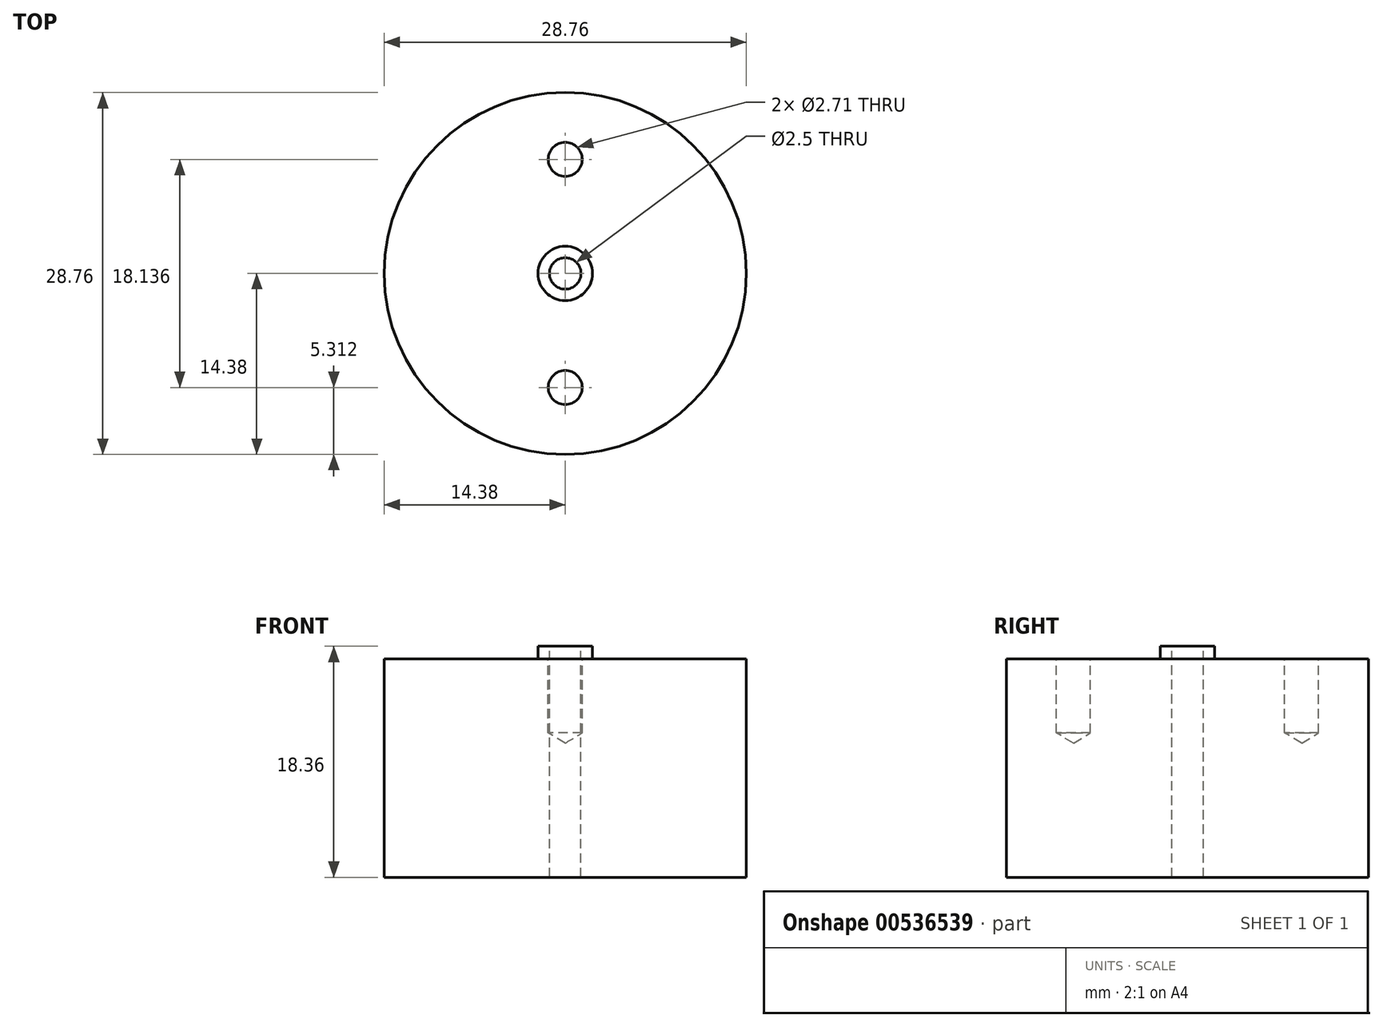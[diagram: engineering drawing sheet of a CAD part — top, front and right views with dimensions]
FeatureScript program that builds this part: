
annotation { "Feature Type Name" : "Feature", "Feature Type Description" : "" }
export const myFeature = defineFeature(function(context is Context, id is Id, definition is map)
    precondition{}
    {
        {
            var Q0;
            Q0=qCreatedBy(makeId("Top.planeOp"),FACE);
            var sketch = newSketch(context, id + "F0", { "sketchPlane" : qUnion([Q0])});
            skCircle(sketch, "E0", {"center": v(0, 0) * mm, "radius": 14.38 * mm});
            skSolve(sketch);
        }
        {
            var Q0;
            Q0 = qSketchRegion(id + "F0", true);
            extrude(context, id + "F1", {"entities" : qUnion([Q0]), "depth" : 17.35 * mm, "offsetDistance" : 25.4 * mm});
        }
        {
            var Q0;
            Q0=makeQuery(id+"F1.opExtrude","CAP_FACE",FACE,{"disambiguationData":[OSD([sQuery(id+"F0.wireOp",EDGE,"E0")])],"isStart":false});
            var sketch = newSketch(context, id + "F2", { "sketchPlane" : qUnion([Q0])});
            skCircle(sketch, "E1", {"center": v(0, 0) * mm, "radius": 2.18 * mm, "construction": true});
            skLineSegment(sketch, "E2.bottom", {"start": v(-7.92, -6.35) * mm, "end": v(11.1, -6.35) * mm, "construction": true});
            skLineSegment(sketch, "E2.top", {"start": v(-7.92, 6.35) * mm, "end": v(11.1, 6.35) * mm, "construction": true});
            skLineSegment(sketch, "E2.left", {"start": v(-7.92, -6.35) * mm, "end": v(-7.92, 6.35) * mm, "construction": true});
            skLineSegment(sketch, "E2.right", {"start": v(11.1, -6.35) * mm, "end": v(11.1, 6.35) * mm, "construction": true});
            skLineSegment(sketch, "E3", {"start": v(-7.92, 0) * mm, "end": v(0, 0) * mm, "construction": true});
            skSolve(sketch);
        }
        {
            var Q0;
            Q0=makeQuery(id+"F1.opExtrude","CAP_FACE",FACE,{"disambiguationData":[OSD([sQuery(id+"F0.wireOp",EDGE,"E0")])],"isStart":false});
            var sketch = newSketch(context, id + "F3", { "sketchPlane" : qUnion([Q0])});
            skPoint(sketch, "E4", {"position": v(0, 9.07) * mm});
            skPoint(sketch, "E5.1.0", {"position": v(0, -9.07) * mm});
            skPoint(sketch, "E5.center", {"position": v(0, 0) * mm});
            skCircle(sketch, "E6", {"center": v(0, 9.07) * mm, "radius": 2.08 * mm, "construction": true});
            skCircle(sketch, "E7", {"center": v(0, -9.07) * mm, "radius": 2.08 * mm, "construction": true});
            skSolve(sketch);
        }
        {
            var Q0;
            Q0=makeQuery(id+"F1.opExtrude","CAP_FACE",FACE,{"disambiguationData":[OSD([sQuery(id+"F0.wireOp",EDGE,"E0")])],"isStart":false});
            var sketch = newSketch(context, id + "F4", { "sketchPlane" : qUnion([Q0])});
            skCircle(sketch, "E8", {"center": v(0, 0) * mm, "radius": 2.16 * mm});
            skSolve(sketch);
        }
        {
            var Q0;
            Q0 = qSketchRegion(id + "F4", true);
            extrude(context, id + "F5", {"entities" : qUnion([Q0]), "operationType" : NewBodyOperationType.ADD, "depth" : 1.02 * mm, "offsetDistance" : 25.4 * mm});
        }
        {
            var Q0;
            Q0=sQuery(id+"F3.wireOp",VERTEX,"E4");
            var Q1;
            Q1=sQuery(id+"F3.wireOp",VERTEX,"E5.2.0");
            var Q2;
            Q2=sQuery(id+"F3.wireOp",VERTEX,"E5.1.0");
            var Q3;
            Q3=makeQuery(id+"F1.opExtrude","SWEPT_BODY",BODY,{"disambiguationData":[OSD([sQuery(id+"F0.wireOp",EDGE,"E0")])]});
            hole(context, id + "F6", {"style" : HoleStyle.SIMPLE, "endStyle" : HoleEndStyle.BLIND, "standardTappedOrClearance" : lookupTablePath({ "standard" : "ANSI", "engagement" : "75%", "pitch" : "32 tpi", "size" : "#6", "type" : "Tapped" }), "standardBlindInLast" : lookupTablePath({ "standard" : "ANSI", "engagement" : "75%", "pitch" : "32 tpi", "size" : "#6", "type" : "Tapped" }), "holeDiameter" : 2.7 * mm, "majorDiameter" : 3.5 * mm, "showTappedDepth" : true, "holeDepth" : 5.87 * mm, "tappedDepth" : 5.08 * mm, "tapClearance" : 1, "startFromSketch" : true, "locations" : qUnion([Q0, Q1, Q2]), "scope" : qUnion([Q3])});
        }
        {
            var Q0;
            Q0=makeQuery(id+"F5.opExtrude","CAP_FACE",FACE,{"disambiguationData":[OSD([sQuery(id+"F4.wireOp",EDGE,"E8")])],"isStart":false});
            var sketch = newSketch(context, id + "F7", { "sketchPlane" : qUnion([Q0])});
            skPoint(sketch, "E9", {"position": v(0, 0) * mm});
            skSolve(sketch);
        }
        {
            var Q0;
            Q0=sQuery(id+"F7.wireOp",VERTEX,"E9");
            var Q1;
            Q1=makeQuery(id+"F1.opExtrude","SWEPT_BODY",BODY,{"disambiguationData":[OSD([sQuery(id+"F0.wireOp",EDGE,"E0")])]});
            hole(context, id + "F8", {"style" : HoleStyle.SIMPLE, "endStyle" : HoleEndStyle.THROUGH, "standardTappedOrClearance" : lookupTablePath({ "standard" : "ISO", "engagement" : "75%", "pitch" : "0.5 mm", "size" : "M3", "type" : "Tapped" }), "standardBlindInLast" : lookupTablePath({ "standard" : "ISO", "engagement" : "75%", "pitch" : "0.5 mm", "size" : "M3", "type" : "Tapped" }), "holeDiameter" : 2.5 * mm, "majorDiameter" : 3 * mm, "showTappedDepth" : true, "isTappedThrough" : true, "tappedDepth" : 5.07 * mm, "tapClearance" : 1, "startFromSketch" : true, "locations" : qUnion([Q0]), "scope" : qUnion([Q1])});
        }
    });
